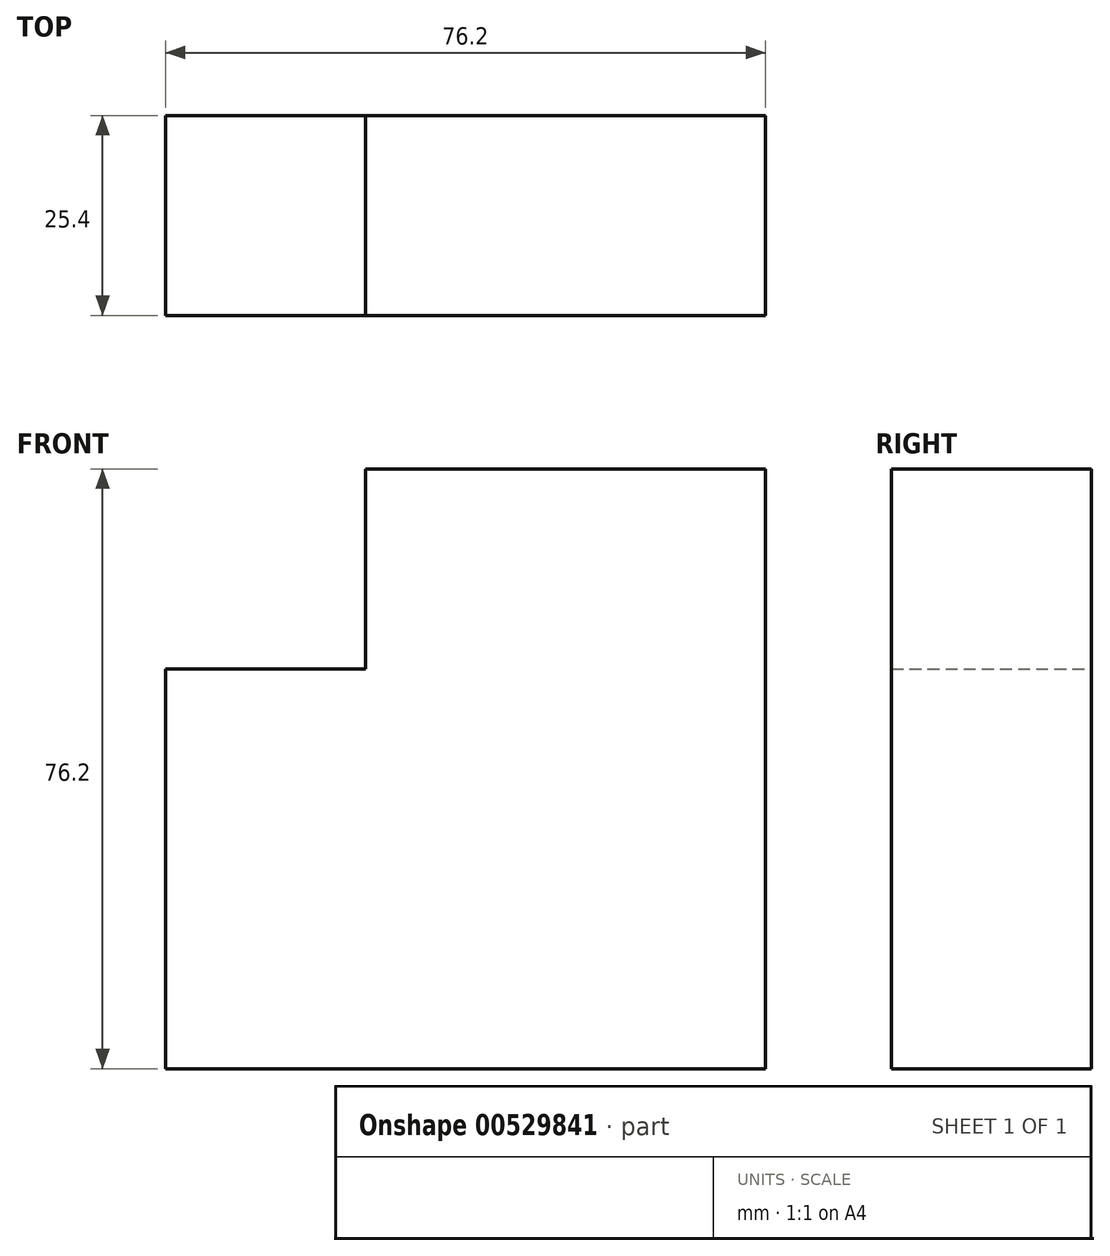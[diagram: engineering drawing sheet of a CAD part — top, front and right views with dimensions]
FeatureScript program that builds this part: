
annotation { "Feature Type Name" : "Feature", "Feature Type Description" : "" }
export const myFeature = defineFeature(function(context is Context, id is Id, definition is map)
    precondition{}
    {
        {
            var Q0;
            Q0=qCreatedBy(makeId("Front.planeOp"),FACE);
            var sketch = newSketch(context, id + "F0", { "sketchPlane" : qUnion([Q0])});
            skLineSegment(sketch, "E0.bottom", {"start": v(0, 0) * mm, "end": v(-25.4, 0) * mm});
            skLineSegment(sketch, "E0.top", {"start": v(0, 25.4) * mm, "end": v(-25.4, 25.4) * mm});
            skLineSegment(sketch, "E0.left", {"start": v(0, 0) * mm, "end": v(0, 25.4) * mm});
            skLineSegment(sketch, "E0.right", {"start": v(-25.4, 0) * mm, "end": v(-25.4, 25.4) * mm});
            skLineSegment(sketch, "E1.bottom", {"start": v(-25.4, 25.4) * mm, "end": v(-50.8, 25.4) * mm});
            skLineSegment(sketch, "E1.top", {"start": v(-25.4, 0) * mm, "end": v(-50.8, 0) * mm});
            skLineSegment(sketch, "E1.left", {"start": v(-25.4, 25.4) * mm, "end": v(-25.4, 0) * mm});
            skLineSegment(sketch, "E1.right", {"start": v(-50.8, 25.4) * mm, "end": v(-50.8, 0) * mm});
            skLineSegment(sketch, "E2.bottom", {"start": v(0, 25.4) * mm, "end": v(25.4, 25.4) * mm});
            skLineSegment(sketch, "E2.top", {"start": v(0, 0) * mm, "end": v(25.4, 0) * mm});
            skLineSegment(sketch, "E2.left", {"start": v(0, 25.4) * mm, "end": v(0, 0) * mm});
            skLineSegment(sketch, "E2.right", {"start": v(25.4, 25.4) * mm, "end": v(25.4, 0) * mm});
            skLineSegment(sketch, "E3.bottom", {"start": v(-25.4, 25.4) * mm, "end": v(0, 25.4) * mm});
            skLineSegment(sketch, "E3.top", {"start": v(-25.4, 50.8) * mm, "end": v(0, 50.8) * mm});
            skLineSegment(sketch, "E3.left", {"start": v(-25.4, 25.4) * mm, "end": v(-25.4, 50.8) * mm});
            skLineSegment(sketch, "E3.right", {"start": v(0, 25.4) * mm, "end": v(0, 50.8) * mm});
            skLineSegment(sketch, "E4.bottom", {"start": v(0, 50.8) * mm, "end": v(25.4, 50.8) * mm});
            skLineSegment(sketch, "E4.left", {"start": v(0, 50.8) * mm, "end": v(0, 25.4) * mm});
            skLineSegment(sketch, "E4.right", {"start": v(25.4, 50.8) * mm, "end": v(25.4, 25.4) * mm});
            skLineSegment(sketch, "E5.top", {"start": v(-25.4, 76.2) * mm, "end": v(0, 76.2) * mm});
            skLineSegment(sketch, "E5.left", {"start": v(-25.4, 50.8) * mm, "end": v(-25.4, 76.2) * mm});
            skLineSegment(sketch, "E5.right", {"start": v(0, 50.8) * mm, "end": v(0, 76.2) * mm});
            skLineSegment(sketch, "E6.bottom", {"start": v(0, 76.2) * mm, "end": v(25.4, 76.2) * mm});
            skLineSegment(sketch, "E6.left", {"start": v(0, 76.2) * mm, "end": v(0, 50.8) * mm});
            skLineSegment(sketch, "E6.right", {"start": v(25.4, 76.2) * mm, "end": v(25.4, 50.8) * mm});
            skLineSegment(sketch, "E7.bottom", {"start": v(-25.4, 50.8) * mm, "end": v(-50.8, 50.8) * mm});
            skLineSegment(sketch, "E7.left", {"start": v(-25.4, 50.8) * mm, "end": v(-25.4, 25.4) * mm});
            skLineSegment(sketch, "E7.right", {"start": v(-50.8, 50.8) * mm, "end": v(-50.8, 25.4) * mm});
            skSolve(sketch);
        }
        {
            var Q0;
            Q0 = qSketchRegion(id + "F0", true);
            extrude(context, id + "F1", {"entities" : qUnion([Q0]), "depth" : 25.4 * mm, "offsetDistance" : 25.4 * mm});
        }
    });
